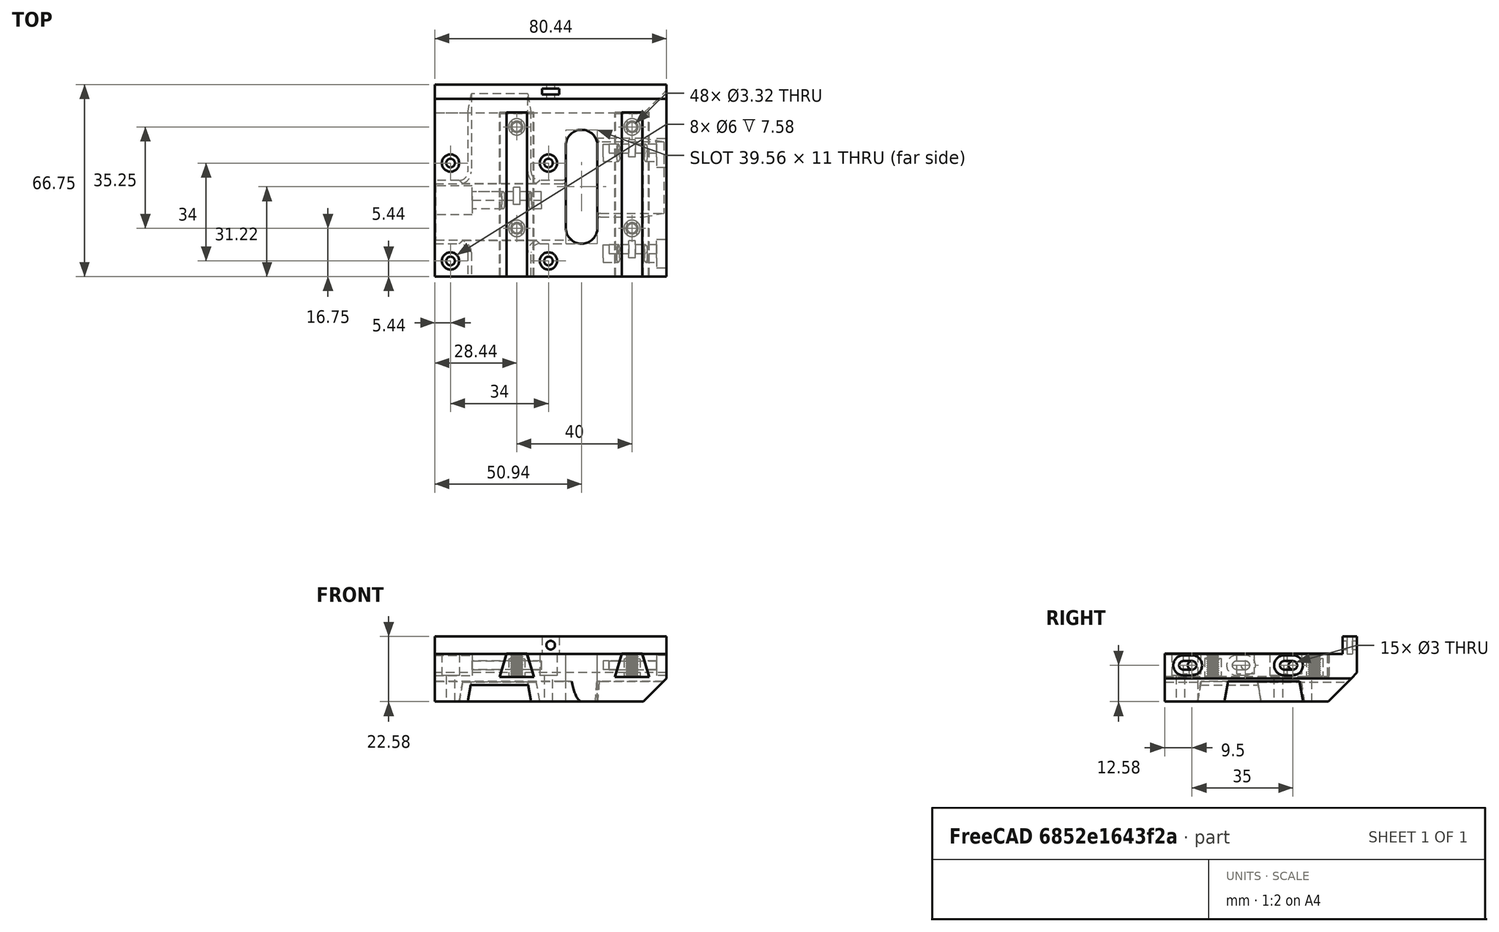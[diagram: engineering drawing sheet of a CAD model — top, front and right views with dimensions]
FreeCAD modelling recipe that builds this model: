
FCSTD DOCUMENT  (FreeCAD 2022.111R28429 (Git))
Label: E2_Adjustable_Plate
License: All rights reserved
LicenseURL: http://en.wikipedia.org/wiki/All_rights_reserved
objects: Sketcher::SketchObject×18, PartDesign::Pocket×16, Sketcher::SketchExport×6, Part::FeaturePython×6, PartDesign::Body×4, PartDesign::FeatureBase×3, Part::SubShapeBinder×2, Part::Extrusion×2, PartDesign::Pad×2, PartDesign::Hole×2, PartDesign::Chamfer×2, PartDesign::SubShapeBinder×1, PartDesign::Fillet×1, Part::Cut×1, App::DocumentObjectGroup×1
note: 115 computed .brp shape members not serialized (recipe doc carries the construction recipe); baked Part::Feature solids carry a one-line shape summary decoded from their .brp

FEATURE [PartDesign::SubShapeBinder] Binder  label="Binder(Pad002)"
  BindCopyOnChange = 0
  BindMode = 0
  ClaimChildren = false
  Context = -> Body001 [Binder.]
  FillStyle = 0
  Fuse = false
  MakeFace = true
  PartialLoad = false
  Refine = true
  Relative = true
  Support = -> [Pad002[Face14]]
  TreeRank = 0
  _Version = 7
FEATURE [Part::SubShapeBinder] Import002  label="Import002(Chamfer002)"
  BindCopyOnChange = 0
  BindMode = 0
  ClaimChildren = false
  FillStyle = 0
  Fuse = false
  MakeFace = false
  PartialLoad = false
  Refine = true
  Relative = true
  Support = -> [Body001[Chamfer002.]]
  TreeRank = 0
  _Version = 7
FEATURE [Part::SubShapeBinder] Import003  label="Import003(M4Holes)"
  BindCopyOnChange = 0
  BindMode = 0
  ClaimChildren = false
  FillStyle = 0
  Fuse = false
  MakeFace = false
  PartialLoad = false
  Refine = true
  Relative = true
  Support = -> [Body001[Export.]]
  TreeRank = 0
  _Version = 7
FEATURE [Sketcher::SketchObject] Sketch015
  ExternalGeometry = -> [Import002,Import003]
  FullyConstrained = true
  Placement = pos=(0,0.1,0) rot=(-1,0,0;4.71239rad)
  TreeRank = 0
  expr: Constraints[20] = Sketch014.Constraints[20]
  expr: Constraints[21] = Sketch014.Constraints[21]
  expr: Constraints[22] = Sketch014.Constraints[22]
  expr: Constraints[23] = Sketch014.Constraints[23]
  expr: Constraints[25] = Sketch014.Constraints[25]
  sketch-geometry (26):
    g0: LineSegment [constr] StartX=28.44 StartY=-3.7e-15 StartZ=0 EndX=28.44 EndY=16.58 EndZ=0
    g1: LineSegment [constr] StartX=68.44 StartY=-3.7e-15 StartZ=0 EndX=68.44 EndY=16.58 EndZ=0
    g2: LineSegment [constr] StartX=24.94 StartY=16.68 StartZ=0 EndX=31.94 EndY=16.68 EndZ=0
    g3: LineSegment [constr] StartX=31.94 StartY=16.68 StartZ=0 EndX=34.44 EndY=8.58 EndZ=0
    g4: LineSegment [constr] StartX=34.44 StartY=8.58 StartZ=0 EndX=22.44 EndY=8.58 EndZ=0
    g5: LineSegment [constr] StartX=22.44 StartY=8.58 StartZ=0 EndX=24.94 EndY=16.68 EndZ=0
    g6: LineSegment [constr] StartX=64.94 StartY=16.68 StartZ=0 EndX=71.94 EndY=16.68 EndZ=0
    g7: LineSegment [constr] StartX=71.94 StartY=16.68 StartZ=0 EndX=74.44 EndY=8.58 EndZ=0
    g8: LineSegment [constr] StartX=74.44 StartY=8.58 StartZ=0 EndX=62.44 EndY=8.58 EndZ=0
    g9: LineSegment [constr] StartX=62.44 StartY=8.58 StartZ=0 EndX=64.94 EndY=16.68 EndZ=0
    g10: LineSegment StartX=22.711 StartY=8.78 StartZ=0 EndX=34.169 EndY=8.78 EndZ=0
    g11: LineSegment StartX=34.169 StartY=8.78 StartZ=0 EndX=31.8233 EndY=16.38 EndZ=0
    g12: LineSegment StartX=31.8233 StartY=16.38 StartZ=0 EndX=25.0567 EndY=16.38 EndZ=0
    g13: LineSegment StartX=25.0567 StartY=16.38 StartZ=0 EndX=22.711 EndY=8.78 EndZ=0
    g14: LineSegment StartX=62.711 StartY=8.78 StartZ=0 EndX=74.169 EndY=8.78 EndZ=0
    g15: LineSegment StartX=74.169 StartY=8.78 StartZ=0 EndX=71.8233 EndY=16.38 EndZ=0
    g16: LineSegment StartX=71.8233 StartY=16.38 StartZ=0 EndX=65.0567 EndY=16.38 EndZ=0
    g17: LineSegment StartX=65.0567 StartY=16.38 StartZ=0 EndX=62.711 EndY=8.78 EndZ=0
    g18: LineSegment [constr] StartX=25.0567 StartY=16.38 StartZ=0 EndX=25.0567 EndY=16.58 EndZ=0
    g19: LineSegment [constr] StartX=25.0567 StartY=16.38 StartZ=0 EndX=24.8656 EndY=16.439 EndZ=0
    g20: LineSegment [constr] StartX=34.169 StartY=8.78 StartZ=0 EndX=34.169 EndY=8.58 EndZ=0
    g21: LineSegment [constr] StartX=34.169 StartY=8.78 StartZ=0 EndX=34.3601 EndY=8.83898 EndZ=0
    g22: LineSegment [constr] StartX=65.0567 StartY=16.38 StartZ=0 EndX=65.0567 EndY=16.58 EndZ=0
    g23: LineSegment [constr] StartX=65.0567 StartY=16.38 StartZ=0 EndX=64.8656 EndY=16.439 EndZ=0
    g24: LineSegment [constr] StartX=74.169 StartY=8.78 StartZ=0 EndX=74.169 EndY=8.58 EndZ=0
    g25: LineSegment [constr] StartX=74.169 StartY=8.78 StartZ=0 EndX=74.3601 EndY=8.83898 EndZ=0
  constraints (74):
    c: PointOnObject(g0,g-6)
    c: Vertical(g0)
    c: PointOnObject(g1,g-6)
    c: Vertical(g1)
    c: Symmetric(g-4,g-4,g1)
    c: Symmetric(g-5,g-5,g0)
    c: Coincident(g2,g3)
    c: Coincident(g3,g4)
    c: Coincident(g4,g5)
    c: Coincident(g5,g2)
    c: Coincident(g6,g7)
    c: Coincident(g7,g8)
    c: Coincident(g8,g9)
    c: Coincident(g9,g6)
    c: Symmetric(g6,g6,g1)
    c: Symmetric(g7,g8,g1)
    c: Symmetric(g2,g2,g0)
    c: Symmetric(g3,g4,g0)
    c: Horizontal(g2,g6)
    c: Equal(g2,g6)
    c: DistanceX(g6,g6) = 7
    c: DistanceY(g-6,g6) = 0.1
    c: DistanceY(g7,g-6) = 8
    c: DistanceX(g8,g8) = 12
    c: Horizontal(g8,g3)
    c: DistanceX(g4,g4) = 12
    c: Horizontal(g10)
    c: Coincident(g10,g11)
    c: Coincident(g11,g12)
    c: Horizontal(g12)
    c: Coincident(g12,g13)
    c: Coincident(g13,g10)
    c: Horizontal(g14)
    c: Coincident(g14,g15)
    c: Coincident(g15,g16)
    c: Horizontal(g16)
    c: Coincident(g16,g17)
    c: Coincident(g17,g14)
    c: Coincident(g18,g12)
    c: PointOnObject(g18,g-6)
    c: Vertical(g18)
    c: Coincident(g19,g12)
    c: PointOnObject(g19,g5)
    c: Coincident(g20,g10)
    c: PointOnObject(g20,g4)
    c: Coincident(g21,g10)
    c: PointOnObject(g21,g3)
    c: Perpendicular(g3,g21)
    c: Perpendicular(g4,g20)
    c: Perpendicular(g5,g19)
    c: Equal(g19,g18)
    c: Equal(g18,g21)
    c: Equal(g21,g20)
    c: Coincident(g22,g16)
    c: PointOnObject(g22,g-6)
    c: Vertical(g22)
    c: Coincident(g23,g16)
    c: PointOnObject(g23,g9)
    c: Coincident(g24,g14)
    c: PointOnObject(g24,g8)
    c: Vertical(g24)
    c: Coincident(g25,g14)
    c: PointOnObject(g25,g7)
    c: Perpendicular(g7,g25)
    c: Perpendicular(g9,g23)
    c: Equal(g23,g22)
    c: Equal(g22,g25)
    c: Equal(g25,g24)
    c: Equal(g22,g20)
    c: Parallel(g11,g3)
    c: Parallel(g5,g13)
    c: Parallel(g17,g9)
    c: Parallel(g15,g7)
    c: DistanceY(g20,g20) = 0.2
FEATURE [Part::Extrusion] Extrude001
  Base = -> Sketch015
  Dir = (0,-1,-2e-16)
  DirMode = 2
  FaceMakerClass = Part::FaceMakerBullseye
  InnerTaperAngle = 0
  InnerTaperAngleRev = 0
  LengthFwd = 56.5
  LengthRev = 0
  Linearize = true
  Reversed = true
  Solid = true
  Symmetric = false
  TreeRank = 0
FEATURE [PartDesign::Body] Body001  label="Slice.0"
  AutoGroupSolids = false
  ExportMode = 0
  Group = -> [Sketch004,Pad002,Binder,Sketch005,Pad003,Sketch006,Pocket003,Sketch007,Sketch009,Pocket006,Pocket007,Sketch011,Pocket,Pocket009,Hole,Export,Sketch013,Pocket010,Pocket011,Pocket012,Hole001,Chamfer001,Chamfer002,Sketch016,Sketch017,Export001,Export002,Export003,Export004,Sketch,Pocket013,Fillet,Export005,Pocket014]
  Origin = -> Origin001
  Tip = -> Pocket014
  TreeRank = 0
  _ExportChildren = -> [Pad002,Binder,Pad003,Pocket003,Pocket006,Pocket007,Pocket,Pocket009,Hole,Pocket010,Pocket011,Pocket012,Hole001,Chamfer001,Chamfer002,Pocket013,Fillet,Pocket014]
  _GroupVersion = 1
FEATURE [Sketcher::SketchObject] Sketch004
  Exports = -> [Export]
  FullyConstrained = true
  MapMode = 5
  Support = -> [XY_Plane001]
  TreeRank = 0
  sketch-geometry (40):
    g0: LineSegment StartX=0 StartY=0 StartZ=0 EndX=80.44 EndY=0 EndZ=0
    g1: LineSegment StartX=80.44 StartY=0 StartZ=0 EndX=80.44 EndY=66.75 EndZ=0
    g2: LineSegment StartX=80.44 StartY=66.75 StartZ=0 EndX=0 EndY=66.75 EndZ=0
    g3: LineSegment StartX=0 StartY=66.75 StartZ=0 EndX=0 EndY=0 EndZ=0
    g4: Circle CenterX=5.44 CenterY=5.44 CenterZ=0 NormalX=0 NormalY=0 NormalZ=1 AngleXU=0 Radius=1.5
    g5: Circle CenterX=39.44 CenterY=5.44 CenterZ=0 NormalX=0 NormalY=0 NormalZ=1 AngleXU=0 Radius=1.5
    g6: Circle CenterX=5.44 CenterY=39.44 CenterZ=0 NormalX=0 NormalY=0 NormalZ=1 AngleXU=0 Radius=1.5
    g7: Circle CenterX=39.44 CenterY=39.44 CenterZ=0 NormalX=0 NormalY=0 NormalZ=1 AngleXU=0 Radius=1.5
    g8: LineSegment [constr] StartX=5.44 StartY=39.44 StartZ=0 EndX=39.44 EndY=39.44 EndZ=0
    g9: LineSegment [constr] StartX=39.44 StartY=39.44 StartZ=0 EndX=39.44 EndY=5.44 EndZ=0
    g10: LineSegment [constr] StartX=39.44 StartY=5.44 StartZ=0 EndX=5.44 EndY=5.44 EndZ=0
    g11: LineSegment [constr] StartX=5.44 StartY=5.44 StartZ=0 EndX=5.44 EndY=39.44 EndZ=0
    g12: Circle [constr] CenterX=28.44 CenterY=52 CenterZ=0 NormalX=0 NormalY=0 NormalZ=1 AngleXU=0 Radius=1.5
    g13: Circle [constr] CenterX=28.44 CenterY=16.75 CenterZ=0 NormalX=0 NormalY=0 NormalZ=1 AngleXU=0 Radius=1.5
    g14: Circle [constr] CenterX=68.44 CenterY=52 CenterZ=0 NormalX=0 NormalY=0 NormalZ=1 AngleXU=0 Radius=1.5
    g15: Circle [constr] CenterX=68.44 CenterY=16.75 CenterZ=0 NormalX=0 NormalY=0 NormalZ=1 AngleXU=0 Radius=1.5
    g16: LineSegment [constr] StartX=28.44 StartY=52 StartZ=0 EndX=68.44 EndY=52 EndZ=0
    g17: LineSegment [constr] StartX=68.44 StartY=52 StartZ=0 EndX=68.44 EndY=16.75 EndZ=0
    g18: LineSegment [constr] StartX=68.44 StartY=16.75 StartZ=0 EndX=28.44 EndY=16.75 EndZ=0
    g19: LineSegment [constr] StartX=28.44 StartY=16.75 StartZ=0 EndX=28.44 EndY=52 EndZ=0
    g20: LineSegment [constr] StartX=22.44 StartY=0 StartZ=0 EndX=34.44 EndY=0 EndZ=0
    g21: LineSegment [constr] StartX=34.44 StartY=0 StartZ=0 EndX=34.44 EndY=57 EndZ=0
    g22: LineSegment [constr] StartX=34.44 StartY=57 StartZ=0 EndX=22.44 EndY=57 EndZ=0
    g23: LineSegment [constr] StartX=22.44 StartY=57 StartZ=0 EndX=22.44 EndY=0 EndZ=0
    g24: LineSegment [constr] StartX=62.44 StartY=0 StartZ=0 EndX=74.44 EndY=0 EndZ=0
    g25: LineSegment [constr] StartX=74.44 StartY=0 StartZ=0 EndX=74.44 EndY=57 EndZ=0
    g26: LineSegment [constr] StartX=74.44 StartY=57 StartZ=0 EndX=62.44 EndY=57 EndZ=0
    g27: LineSegment [constr] StartX=62.44 StartY=57 StartZ=0 EndX=62.44 EndY=0 EndZ=0
    g28: LineSegment [constr] StartX=28.44 StartY=52 StartZ=0 EndX=28.44 EndY=57 EndZ=0
    g29: LineSegment [constr] StartX=68.44 StartY=52 StartZ=0 EndX=68.44 EndY=57 EndZ=0
    g30: ArcOfCircle CenterX=50.94 CenterY=45.5 CenterZ=0 NormalX=0 NormalY=0 NormalZ=1 AngleXU=0 Radius=5.5 StartAngle=0 EndAngle=3.14159
    g31: ArcOfCircle CenterX=50.94 CenterY=16.94 CenterZ=0 NormalX=0 NormalY=0 NormalZ=1 AngleXU=0 Radius=5.5 StartAngle=3.14159 EndAngle=6.28319
    g32: LineSegment StartX=45.44 StartY=45.5 StartZ=0 EndX=45.44 EndY=16.94 EndZ=0
    g33: LineSegment StartX=56.44 StartY=45.5 StartZ=0 EndX=56.44 EndY=16.94 EndZ=0
    g34: LineSegment [constr] StartX=45.44 StartY=16.94 StartZ=0 EndX=39.44 EndY=16.94 EndZ=0
    g35: LineSegment [constr] StartX=56.44 StartY=16.94 StartZ=0 EndX=62.44 EndY=16.94 EndZ=0
    g36: LineSegment [constr] StartX=34.44 StartY=57 StartZ=0 EndX=62.44 EndY=57 EndZ=0
    g37: LineSegment [constr] StartX=50.94 StartY=57 StartZ=0 EndX=50.94 EndY=51 EndZ=0
    g38: LineSegment [constr] StartX=39.44 StartY=5.44 StartZ=0 EndX=62.44 EndY=5.44 EndZ=0
    g39: LineSegment [constr] StartX=50.94 StartY=5.44 StartZ=0 EndX=50.94 EndY=11.44 EndZ=0
  constraints (108):
    c: Coincident(g0,g1)
    c: Coincident(g1,g2)
    c: Coincident(g2,g3)
    c: Coincident(g3,g0)
    c: Horizontal(g0)
    c: Horizontal(g2)
    c: Vertical(g1)
    c: Vertical(g3)
    c: Coincident(g0,g-1)
    c: DistanceY(g3,g3) = 66.75
    c: Coincident(g8,g9)
    c: Coincident(g9,g10)
    c: Coincident(g10,g11)
    c: Coincident(g11,g8)
    c: Horizontal(g8)
    c: Horizontal(g10)
    c: Vertical(g9)
    c: Vertical(g11)
    c: Coincident(g8,g6)
    c: Coincident(g9,g5)
    c: Coincident(g7,g8)
    c: Coincident(g4,g10)
    c: Equal(g10,g11)
    c: DistanceY(g11,g11) = 34
    c: DistanceX(g0,g4) = 5.44
    c: DistanceY(g0,g4) = 5.44
    c: Diameter(g4) = 3
    c: Equal(g4,g5)
    c: Equal(g4,g7)
    c: Equal(g4,g6)
    c: Coincident(g16,g17)
    c: Coincident(g17,g18)
    c: Coincident(g18,g19)
    c: Coincident(g19,g16)
    c: Horizontal(g16)
    c: Horizontal(g18)
    c: Vertical(g17)
    c: Vertical(g19)
    c: Coincident(g16,g12)
    c: Coincident(g17,g15)
    c: Coincident(g13,g18)
    c: Coincident(g14,g16)
    c: DistanceX(g16,g16) = 40
    c: DistanceY(g17,g17) = 35.25
    c: Diameter(g13) = 3
    c: Equal(g13,g15)
    c: Equal(g13,g14)
    c: Equal(g13,g12)
    c: DistanceY(g0,g13) = 16.75
    c: DistanceX(g4,g13) = 23
    c: DistanceX(g15,g0) = 12
    c: Coincident(g20,g21)
    c: Coincident(g21,g22)
    c: Coincident(g22,g23)
    c: Coincident(g23,g20)
    c: Horizontal(g20)
    c: Horizontal(g22)
    c: Vertical(g21)
    c: Vertical(g23)
    c: PointOnObject(g20,g0)
    c: Coincident(g24,g25)
    c: Coincident(g25,g26)
    c: Coincident(g26,g27)
    c: Coincident(g27,g24)
    c: Horizontal(g24)
    c: Horizontal(g26)
    c: Vertical(g25)
    c: Vertical(g27)
    c: PointOnObject(g24,g0)
    c: Equal(g22,g26)
    c: DistanceX(g26,g26) = 12
    c: DistanceY(g25,g25) = 57
    c: Horizontal(g26,g21)
    c: Coincident(g28,g12)
    c: Vertical(g28)
    c: Coincident(g29,g14)
    c: Vertical(g29)
    c: Symmetric(g26,g25,g29)
    c: Symmetric(g22,g21,g28)
    c: Tangent(g30,g33) = 1.5708
    c: Tangent(g30,g32) = -1.5708
    c: Tangent(g32,g31) = -1.5708
    c: Tangent(g33,g31) = 1.5708
    c: Vertical(g32)
    c: Coincident(g34,g31)
    c: PointOnObject(g34,g9)
    c: Coincident(g35,g31)
    c: PointOnObject(g35,g27)
    c: Horizontal(g35)
    c: Horizontal(g34)
    c: Equal(g34,g35)
    c: DistanceX(g35,g35) = 6
    c: Vertical(g33)
    c: Coincident(g36,g21)
    c: Coincident(g36,g26)
    c: PointOnObject(g37,g36)
    c: PointOnObject(g37,g30)
    c: Vertical(g37)
    c: Vertical(g37,g30)
    c: Equal(g37,g35)
    c: Coincident(g38,g5)
    c: PointOnObject(g38,g27)
    c: Horizontal(g38)
    c: PointOnObject(g39,g38)
    c: PointOnObject(g39,g31)
    c: Vertical(g39)
    c: Vertical(g39,g31)
    c: Equal(g34,g39)
FEATURE [PartDesign::Pad] Pad002
  ClaimChildren = false
  Direction = (1,1,1)
  Fit = 0
  FitJoin = 0
  InnerFit = 0
  InnerFitJoin = 0
  InnerTaperAngle = 0
  InnerTaperAngleRev = 0
  Length = 16.58
  Length2 = 100
  Linearize = true
  NewSolid = false
  Profile = -> Sketch004
  Refine = true
  Suppress = false
  TreeRank = 0
  Type = 0
  _ProfileBasedVersion = 1
FEATURE [Sketcher::SketchObject] Sketch005
  ExternalGeometry = -> [Pad002]
  FullyConstrained = true
  MapMode = 5
  Placement = pos=(0,0,16.58) rot=(0,0,1;0rad)
  Support = -> [Binder]
  TreeRank = 0
  sketch-geometry (4):
    g0: LineSegment StartX=0 StartY=66.75 StartZ=0 EndX=80.44 EndY=66.75 EndZ=0
    g1: LineSegment StartX=80.44 StartY=66.75 StartZ=0 EndX=80.44 EndY=61.75 EndZ=0
    g2: LineSegment StartX=80.44 StartY=61.75 StartZ=0 EndX=0 EndY=61.75 EndZ=0
    g3: LineSegment StartX=0 StartY=61.75 StartZ=0 EndX=0 EndY=66.75 EndZ=0
  constraints (10):
    c: Coincident(g0,g1)
    c: Coincident(g1,g2)
    c: Coincident(g2,g3)
    c: Coincident(g3,g0)
    c: Horizontal(g2)
    c: Vertical(g1)
    c: Vertical(g3)
    c: Coincident(g0,g-3)
    c: Coincident(g0,g-3)
    c: DistanceY(g1,g1) = 5
FEATURE [PartDesign::Pad] Pad003
  BaseFeature = -> Pad002
  ClaimChildren = false
  Direction = (1,1,1)
  Fit = 0
  FitJoin = 0
  InnerFit = 0
  InnerFitJoin = 0
  InnerTaperAngle = 0
  InnerTaperAngleRev = 0
  Length = 6
  Length2 = 100
  Linearize = true
  NewSolid = false
  Profile = -> Sketch005
  Refine = true
  Suppress = false
  TreeRank = 0
  Type = 0
  _ProfileBasedVersion = 1
FEATURE [Sketcher::SketchObject] Sketch006
  ExternalGeometry = -> [Pad003]
  FullyConstrained = true
  MapMode = 5
  Placement = pos=(0,66.75,0) rot=(0,0.707107,0.707107;3.14159rad)
  Support = -> [Pad003]
  TreeRank = 0
  sketch-geometry (2):
    g0: Circle CenterX=-40.22 CenterY=19.58 CenterZ=0 NormalX=0 NormalY=0 NormalZ=1 AngleXU=0 Radius=1.5
    g1: LineSegment [constr] StartX=-40.22 StartY=19.58 StartZ=0 EndX=-40.22 EndY=22.58 EndZ=0
  constraints (5):
    c: Diameter(g0) = 3
    c: Coincident(g1,g0)
    c: Vertical(g1)
    c: DistanceY(g1,g1) = 3
    c: Symmetric(g-3,g-3,g1)
FEATURE [PartDesign::Pocket] Pocket003
  BaseFeature = -> Pad003
  ClaimChildren = false
  Fit = 0
  FitJoin = 0
  InnerFit = 0
  InnerFitJoin = 0
  InnerTaperAngle = 0
  InnerTaperAngleRev = 0
  Length = 5
  Length2 = 100
  Linearize = true
  NewSolid = false
  Profile = -> Sketch006
  Refine = true
  Suppress = false
  TreeRank = 0
  Type = 2
  _ProfileBasedVersion = 1
FEATURE [Sketcher::SketchObject] Sketch007
  ExternalGeometry = -> [Pocket003]
  FullyConstrained = true
  MapMode = 5
  Placement = pos=(0,0,22.58) rot=(0,0,1;0rad)
  Support = -> [Pocket003]
  TreeRank = 0
  sketch-geometry (8):
    g0: LineSegment StartX=37.22 StartY=65.25 StartZ=0 EndX=43.22 EndY=65.25 EndZ=0
    g1: LineSegment StartX=43.22 StartY=65.25 StartZ=0 EndX=43.22 EndY=63.25 EndZ=0
    g2: LineSegment StartX=43.22 StartY=63.25 StartZ=0 EndX=37.22 EndY=63.25 EndZ=0
    g3: LineSegment StartX=37.22 StartY=63.25 StartZ=0 EndX=37.22 EndY=65.25 EndZ=0
    g4: LineSegment [constr] StartX=40.22 StartY=66.75 StartZ=0 EndX=40.22 EndY=64.25 EndZ=0
    g5: LineSegment [constr] StartX=40.22 StartY=64.25 StartZ=0 EndX=40.22 EndY=61.75 EndZ=0
    g6: LineSegment [constr] StartX=40.22 StartY=64.25 StartZ=0 EndX=37.22 EndY=64.25 EndZ=0
    g7: LineSegment [constr] StartX=40.22 StartY=64.25 StartZ=0 EndX=43.22 EndY=64.25 EndZ=0
  constraints (23):
    c: Coincident(g0,g1)
    c: Coincident(g1,g2)
    c: Coincident(g2,g3)
    c: Coincident(g3,g0)
    c: Horizontal(g0)
    c: Horizontal(g2)
    c: Vertical(g1)
    c: Vertical(g3)
    c: DistanceY(g1,g1) = 2
    c: DistanceX(g0,g0) = 6
    c: Vertical(g4)
    c: Coincident(g5,g4)
    c: PointOnObject(g5,g-4)
    c: Vertical(g5)
    c: Coincident(g6,g4)
    c: PointOnObject(g6,g3)
    c: Coincident(g7,g4)
    c: Horizontal(g7)
    c: Horizontal(g6)
    c: Equal(g6,g7)
    c: Equal(g5,g4)
    c: Symmetric(g1,g0,g7)
    c: Symmetric(g-3,g-3,g4)
FEATURE [Sketcher::SketchObject] Sketch009
  Exports = -> [Export001,Export002]
  FullyConstrained = true
  MapMode = 5
  Placement = pos=(0,0,0) rot=(0.57735,-0.57735,-0.57735;2.0944rad)
  Support = -> [Pocket003]
  TreeRank = 0
  sketch-geometry (9):
    g0: ArcOfCircle [constr] CenterX=-28 CenterY=12.58 CenterZ=0 NormalX=0 NormalY=0 NormalZ=1 AngleXU=0 Radius=1.5 StartAngle=1.5708 EndAngle=4.71239
    g1: ArcOfCircle [constr] CenterX=-25 CenterY=12.58 CenterZ=0 NormalX=0 NormalY=0 NormalZ=1 AngleXU=0 Radius=1.5 StartAngle=4.71239 EndAngle=7.85398
    g2: LineSegment [constr] StartX=-28 StartY=11.08 StartZ=0 EndX=-25 EndY=11.08 EndZ=0
    g3: LineSegment [constr] StartX=-28 StartY=14.08 StartZ=0 EndX=-25 EndY=14.08 EndZ=0
    g4: ArcOfCircle CenterX=-28 CenterY=12.58 CenterZ=0 NormalX=0 NormalY=0 NormalZ=1 AngleXU=0 Radius=3.5 StartAngle=1.5708 EndAngle=4.71239
    g5: ArcOfCircle CenterX=-25 CenterY=12.58 CenterZ=0 NormalX=0 NormalY=0 NormalZ=1 AngleXU=0 Radius=3.5 StartAngle=4.71239 EndAngle=7.85398
    g6: LineSegment StartX=-28 StartY=9.08 StartZ=0 EndX=-25 EndY=9.08 EndZ=0
    g7: LineSegment StartX=-28 StartY=16.08 StartZ=0 EndX=-25 EndY=16.08 EndZ=0
    g8: Circle [constr] CenterX=-28 CenterY=12.58 CenterZ=0 NormalX=0 NormalY=0 NormalZ=1 AngleXU=0 Radius=1.5
  constraints (20):
    c: Tangent(g0,g3) = 1.5708
    c: Tangent(g0,g2) = -1.5708
    c: Tangent(g2,g1) = -1.5708
    c: Tangent(g3,g1) = 1.5708
    c: Horizontal(g2)
    c: Equal(g0,g1)
    c: Tangent(g4,g7) = 1.5708
    c: Tangent(g4,g6) = -1.5708
    c: Tangent(g6,g5) = -1.5708
    c: Tangent(g7,g5) = 1.5708
    c: Horizontal(g6)
    c: Coincident(g4,g0)
    c: Coincident(g1,g5)
    c: Diameter(g1) = 3
    c: Diameter(g5) = 7
    c: DistanceX(g0,g1) = 3
    c: DistanceX(g1,g-1) = 25
    c: DistanceY(g-1,g1) = 12.58
    c: Coincident(g8,g0)
    c: Equal(g8,g0)
FEATURE [PartDesign::Pocket] Pocket006
  BaseFeature = -> Pocket003
  ClaimChildren = false
  Fit = 0
  FitJoin = 0
  InnerFit = 0
  InnerFitJoin = 0
  InnerTaperAngle = 0
  InnerTaperAngleRev = 0
  Length = 6
  Length2 = 100
  Linearize = true
  NewSolid = false
  Profile = -> Sketch007
  Refine = true
  Suppress = false
  TreeRank = 0
  Type = 0
  _ProfileBasedVersion = 1
FEATURE [PartDesign::Pocket] Pocket007
  BaseFeature = -> Pocket006
  ClaimChildren = false
  Fit = 0
  FitJoin = 0
  InnerFit = 0
  InnerFitJoin = 0
  InnerTaperAngle = 0
  InnerTaperAngleRev = 0
  Length = 13
  Length2 = 100
  Linearize = true
  NewSolid = false
  Profile = -> Sketch009
  Refine = true
  Suppress = false
  TreeRank = 0
  Type = 0
  _ProfileBasedVersion = 1
FEATURE [Sketcher::SketchObject] Sketch011
  Exports = -> [Export003,Export004]
  FullyConstrained = true
  MapMode = 5
  Placement = pos=(80.44,0,0) rot=(0.57735,0.57735,0.57735;2.0944rad)
  Support = -> [Pocket007]
  TreeRank = 0
  sketch-geometry (18):
    g0: ArcOfCircle [constr] CenterX=6.5 CenterY=12.58 CenterZ=0 NormalX=0 NormalY=0 NormalZ=1 AngleXU=0 Radius=1.5 StartAngle=1.5708 EndAngle=4.71239
    g1: ArcOfCircle [constr] CenterX=9.5 CenterY=12.58 CenterZ=0 NormalX=0 NormalY=0 NormalZ=1 AngleXU=0 Radius=1.5 StartAngle=4.71239 EndAngle=7.85398
    g2: LineSegment [constr] StartX=6.5 StartY=11.08 StartZ=0 EndX=9.5 EndY=11.08 EndZ=0
    g3: LineSegment [constr] StartX=6.5 StartY=14.08 StartZ=0 EndX=9.5 EndY=14.08 EndZ=0
    g4: ArcOfCircle CenterX=6.5 CenterY=12.58 CenterZ=0 NormalX=0 NormalY=0 NormalZ=1 AngleXU=0 Radius=3.5 StartAngle=1.5708 EndAngle=4.71239
    g5: ArcOfCircle CenterX=9.5 CenterY=12.58 CenterZ=0 NormalX=0 NormalY=0 NormalZ=1 AngleXU=0 Radius=3.5 StartAngle=4.71239 EndAngle=7.85398
    g6: LineSegment StartX=6.5 StartY=9.08 StartZ=0 EndX=9.5 EndY=9.08 EndZ=0
    g7: LineSegment StartX=6.5 StartY=16.08 StartZ=0 EndX=9.5 EndY=16.08 EndZ=0
    g8: ArcOfCircle [constr] CenterX=41.5 CenterY=12.58 CenterZ=0 NormalX=0 NormalY=0 NormalZ=1 AngleXU=0 Radius=1.5 StartAngle=1.5708 EndAngle=4.71239
    g9: ArcOfCircle [constr] CenterX=44.5 CenterY=12.58 CenterZ=0 NormalX=0 NormalY=0 NormalZ=1 AngleXU=0 Radius=1.5 StartAngle=4.71239 EndAngle=7.85398
    g10: LineSegment [constr] StartX=41.5 StartY=11.08 StartZ=0 EndX=44.5 EndY=11.08 EndZ=0
    g11: LineSegment [constr] StartX=41.5 StartY=14.08 StartZ=0 EndX=44.5 EndY=14.08 EndZ=0
    g12: ArcOfCircle CenterX=41.5 CenterY=12.58 CenterZ=0 NormalX=0 NormalY=0 NormalZ=1 AngleXU=0 Radius=3.5 StartAngle=1.5708 EndAngle=4.71239
    g13: ArcOfCircle CenterX=44.5 CenterY=12.58 CenterZ=0 NormalX=0 NormalY=0 NormalZ=1 AngleXU=0 Radius=3.5 StartAngle=4.71239 EndAngle=7.85398
    g14: LineSegment StartX=41.5 StartY=9.08 StartZ=0 EndX=44.5 EndY=9.08 EndZ=0
    g15: LineSegment StartX=41.5 StartY=16.08 StartZ=0 EndX=44.5 EndY=16.08 EndZ=0
    g16: Circle [constr] CenterX=9.5 CenterY=12.58 CenterZ=0 NormalX=0 NormalY=0 NormalZ=1 AngleXU=0 Radius=1.5
    g17: Circle [constr] CenterX=44.5 CenterY=12.58 CenterZ=0 NormalX=0 NormalY=0 NormalZ=1 AngleXU=0 Radius=1.5
  constraints (40):
    c: Tangent(g0,g3) = 1.5708
    c: Tangent(g0,g2) = -1.5708
    c: Tangent(g2,g1) = -1.5708
    c: Tangent(g3,g1) = 1.5708
    c: Horizontal(g2)
    c: Equal(g0,g1)
    c: Tangent(g4,g7) = 1.5708
    c: Tangent(g4,g6) = -1.5708
    c: Tangent(g6,g5) = -1.5708
    c: Tangent(g7,g5) = 1.5708
    c: Horizontal(g6)
    c: Coincident(g4,g0)
    c: Tangent(g8,g11) = 1.5708
    c: Tangent(g8,g10) = -1.5708
    c: Tangent(g10,g9) = -1.5708
    c: Tangent(g11,g9) = 1.5708
    c: Horizontal(g10)
    c: Equal(g8,g9)
    c: Tangent(g12,g15) = 1.5708
    c: Tangent(g12,g14) = -1.5708
    c: Tangent(g14,g13) = -1.5708
    c: Tangent(g15,g13) = 1.5708
    c: Horizontal(g14)
    c: Coincident(g12,g8)
    c: Coincident(g9,g13)
    c: Coincident(g1,g5)
    c: Horizontal(g1,g8)
    c: Diameter(g1) = 3
    c: Equal(g1,g8)
    c: Diameter(g5) = 7
    c: Equal(g5,g12)
    c: DistanceX(g8,g9) = 3
    c: DistanceX(g0,g1) = 3
    c: DistanceX(g-1,g0) = 6.5
    c: DistanceX(g-1,g8) = 41.5
    c: DistanceY(g-1,g0) = 12.58
    c: Coincident(g16,g5)
    c: Equal(g16,g1)
    c: Coincident(g17,g13)
    c: Equal(g17,g9)
FEATURE [PartDesign::Pocket] Pocket009
  BaseFeature = -> Pocket
  ClaimChildren = false
  Fit = 0
  FitJoin = 0
  InnerFit = 0
  InnerFitJoin = 0
  InnerTaperAngle = 0
  InnerTaperAngleRev = 0
  Length = 3.5
  Length2 = 100
  Linearize = true
  NewSolid = false
  Profile = -> Sketch011
  Refine = true
  Suppress = false
  TreeRank = 0
  Type = 0
  _ProfileBasedVersion = 1
FEATURE [PartDesign::Hole] Hole
  BaseFeature = -> Pocket009
  ClaimChildren = false
  CustomThreadClearance = 0
  Depth = 7.58
  DepthType = 0
  Diameter = 6
  DrillForDepth = false
  DrillPoint = 0
  DrillPointAngle = 118
  Fit = 0
  FitJoin = 0
  HoleCutCountersinkAngle = 90
  HoleCutCustomValues = false
  HoleCutDepth = 0
  HoleCutDiameter = 6.1
  HoleCutType = 0
  InnerFit = 0
  InnerFitJoin = 0
  ModelThread = false
  NewSolid = false
  Profile = -> Pocket009 [Edge39,Edge44,Vertex33,Edge37,Edge38]
  Refine = true
  Suppress = false
  Tapered = false
  TaperedAngle = 90
  ThreadClass = 0
  ThreadDepth = 7.58
  ThreadDepthType = 0
  ThreadDirection = 0
  ThreadFit = 0
  ThreadSize = 0
  ThreadType = 0
  Threaded = false
  TreeRank = 0
  UseCustomThreadClearance = false
  _ProfileBasedVersion = 1
FEATURE [Sketcher::SketchExport] Export  label="M4Holes"
  Base = -> Sketch004
  BaseRefs = -> Sketch004 [edge13,edge15,edge16,edge14]
  Refs = ;g13.edge13 | ;g15.edge15 | ;g16.edge16 | ;g14.edge14
  SyncPlacement = true
  TreeRank = 0
FEATURE [Sketcher::SketchObject] Sketch013
  ExternalGeometry = -> [Export]
  FullyConstrained = true
  MapMode = 5
  Placement = pos=(0,0,16.58) rot=(0,0,1;0rad)
  Support = -> [Hole]
  TreeRank = 0
  sketch-geometry (4):
    g0: Circle CenterX=68.44 CenterY=16.75 CenterZ=0 NormalX=0 NormalY=0 NormalZ=1 AngleXU=0 Radius=1.5
    g1: Circle CenterX=28.44 CenterY=16.75 CenterZ=0 NormalX=0 NormalY=0 NormalZ=1 AngleXU=0 Radius=1.5
    g2: Circle CenterX=68.44 CenterY=52 CenterZ=0 NormalX=0 NormalY=0 NormalZ=1 AngleXU=0 Radius=1.5
    g3: Circle CenterX=28.44 CenterY=52 CenterZ=0 NormalX=0 NormalY=0 NormalZ=1 AngleXU=0 Radius=1.5
  constraints (8):
    c: Coincident(g0,g-4)
    c: Coincident(g1,g-3)
    c: Coincident(g2,g-5)
    c: Equal(g2,g-5)
    c: Equal(g-4,g0)
    c: Equal(g-3,g1)
    c: Coincident(g3,g-6)
    c: Equal(g-6,g3)
FEATURE [PartDesign::Hole] Hole001
  BaseFeature = -> Pocket012
  ClaimChildren = false
  CustomThreadClearance = 0
  Depth = 8
  DepthType = 0
  Diameter = 3.322
  DrillForDepth = false
  DrillPoint = 0
  DrillPointAngle = 118
  Fit = 0
  FitJoin = 0
  HoleCutCountersinkAngle = 90
  HoleCutCustomValues = false
  HoleCutDepth = 0
  HoleCutDiameter = 6.1
  HoleCutType = 0
  InnerFit = 0
  InnerFitJoin = 0
  ModelThread = true
  NewSolid = false
  Profile = -> Sketch013
  Refine = true
  Suppress = false
  Tapered = false
  TaperedAngle = 90
  ThreadClass = 0
  ThreadDepth = 8
  ThreadDepthType = 0
  ThreadDirection = 0
  ThreadFit = 0
  ThreadSize = 11
  ThreadType = 1
  Threaded = true
  TreeRank = 0
  UseCustomThreadClearance = false
  _ProfileBasedVersion = 1
FEATURE [PartDesign::Chamfer] Chamfer001
  Angle = 45
  Base = -> Hole001 [Edge14]
  BaseFeature = -> Hole001
  ChamferType = 0
  FlipDirection = false
  NewSolid = false
  Refine = true
  Size = 8
  Size2 = 1
  SupportTransform = false
  Suppress = false
  TreeRank = 0
FEATURE [PartDesign::Chamfer] Chamfer002
  Angle = 45
  Base = -> Chamfer001 [Edge64]
  BaseFeature = -> Chamfer001
  ChamferType = 0
  FlipDirection = false
  NewSolid = false
  Refine = true
  Size = 10
  Size2 = 1
  SupportTransform = false
  Suppress = false
  TreeRank = 0
FEATURE [Sketcher::SketchObject] Sketch014
  ExternalGeometry = -> [Import002,Import003]
  FullyConstrained = true
  MapMode = 5
  Placement = pos=(0,0,0) rot=(1,0,0;1.5708rad)
  Support = -> [Chamfer002]
  TreeRank = 0
  sketch-geometry (10):
    g0: LineSegment [constr] StartX=28.44 StartY=3.7e-15 StartZ=0 EndX=28.44 EndY=16.58 EndZ=0
    g1: LineSegment [constr] StartX=68.44 StartY=3.7e-15 StartZ=0 EndX=68.44 EndY=16.58 EndZ=0
    g2: LineSegment StartX=24.94 StartY=16.68 StartZ=0 EndX=31.94 EndY=16.68 EndZ=0
    g3: LineSegment StartX=31.94 StartY=16.68 StartZ=0 EndX=34.44 EndY=8.58 EndZ=0
    g4: LineSegment StartX=34.44 StartY=8.58 StartZ=0 EndX=22.44 EndY=8.58 EndZ=0
    g5: LineSegment StartX=22.44 StartY=8.58 StartZ=0 EndX=24.94 EndY=16.68 EndZ=0
    g6: LineSegment StartX=64.94 StartY=16.68 StartZ=0 EndX=71.94 EndY=16.68 EndZ=0
    g7: LineSegment StartX=71.94 StartY=16.68 StartZ=0 EndX=74.44 EndY=8.58 EndZ=0
    g8: LineSegment StartX=74.44 StartY=8.58 StartZ=0 EndX=62.44 EndY=8.58 EndZ=0
    g9: LineSegment StartX=62.44 StartY=8.58 StartZ=0 EndX=64.94 EndY=16.68 EndZ=0
  constraints (26):
    c: PointOnObject(g0,g-6)
    c: Vertical(g0)
    c: PointOnObject(g1,g-6)
    c: Vertical(g1)
    c: Symmetric(g-4,g-4,g1)
    c: Symmetric(g-5,g-5,g0)
    c: Coincident(g2,g3)
    c: Coincident(g3,g4)
    c: Coincident(g4,g5)
    c: Coincident(g5,g2)
    c: Coincident(g6,g7)
    c: Coincident(g7,g8)
    c: Coincident(g8,g9)
    c: Coincident(g9,g6)
    c: Symmetric(g6,g6,g1)
    c: Symmetric(g7,g8,g1)
    c: Symmetric(g2,g2,g0)
    c: Symmetric(g3,g4,g0)
    c: Horizontal(g2,g6)
    c: Equal(g2,g6)
    c: DistanceX(g6,g6) = 7
    c: DistanceY(g-6,g6) = 0.1
    c: DistanceY(g7,g-6) = 8
    c: DistanceX(g8,g8) = 12
    c: Horizontal(g8,g3)
    c: DistanceX(g4,g4) = 12
FEATURE [Sketcher::SketchObject] Sketch016
  AttachmentOffset = pos=(0,0,-12) rot=(0,0,1;0rad)
  ExternalGeometry = -> [Chamfer002,Export004]
  FullyConstrained = true
  MapMode = 5
  Placement = pos=(68.44,0,0) rot=(0.57735,0.57735,0.57735;2.0944rad)
  Support = -> [Chamfer002]
  TreeRank = 0
  sketch-geometry (10):
    g0: LineSegment StartX=6.5 StartY=16.58 StartZ=0 EndX=12.5 EndY=16.58 EndZ=0
    g1: LineSegment StartX=12.5 StartY=16.58 StartZ=0 EndX=12.5 EndY=9.58 EndZ=0
    g2: LineSegment StartX=12.5 StartY=9.58 StartZ=0 EndX=6.5 EndY=9.58 EndZ=0
    g3: LineSegment StartX=6.5 StartY=9.58 StartZ=0 EndX=6.5 EndY=16.58 EndZ=0
    g4: LineSegment StartX=41.5 StartY=16.58 StartZ=0 EndX=47.5 EndY=16.58 EndZ=0
    g5: LineSegment StartX=47.5 StartY=16.58 StartZ=0 EndX=47.5 EndY=9.58 EndZ=0
    g6: LineSegment StartX=47.5 StartY=9.58 StartZ=0 EndX=41.5 EndY=9.58 EndZ=0
    g7: LineSegment StartX=41.5 StartY=9.58 StartZ=0 EndX=41.5 EndY=16.58 EndZ=0
    g8: LineSegment [constr] StartX=44.5 StartY=9.58 StartZ=0 EndX=44.5 EndY=16.58 EndZ=0
    g9: LineSegment [constr] StartX=9.5 StartY=9.58 StartZ=0 EndX=9.5 EndY=16.58 EndZ=0
  constraints (30):
    c: Coincident(g0,g1)
    c: Coincident(g1,g2)
    c: Coincident(g2,g3)
    c: Coincident(g3,g0)
    c: Horizontal(g0)
    c: Horizontal(g2)
    c: Vertical(g1)
    c: Vertical(g3)
    c: Coincident(g4,g5)
    c: Coincident(g5,g6)
    c: Coincident(g6,g7)
    c: Coincident(g7,g4)
    c: Horizontal(g4)
    c: Horizontal(g6)
    c: Vertical(g5)
    c: Vertical(g7)
    c: PointOnObject(g8,g-3)
    c: Vertical(g8)
    c: PointOnObject(g9,g-3)
    c: Vertical(g9)
    c: Symmetric(g2,g1,g9)
    c: Symmetric(g6,g5,g8)
    c: Equal(g2,g6)
    c: DistanceX(g2,g2) = 6
    c: PointOnObject(g0,g-3)
    c: Horizontal(g0,g4)
    c: Horizontal(g1,g6)
    c: PointOnObject(g-4,g9)
    c: PointOnObject(g-5,g8)
    c: DistanceY(g9,g-4) = 3
FEATURE [Sketcher::SketchObject] Sketch017
  AttachmentOffset = pos=(0,0,-52) rot=(0,0,1;0rad)
  ExternalGeometry = -> [Export002,Pocket010]
  FullyConstrained = true
  MapMode = 5
  Placement = pos=(28.44,0,0) rot=(0.57735,0.57735,0.57735;2.0944rad)
  TreeRank = 0
  sketch-geometry (5):
    g0: LineSegment StartX=25 StartY=16.58 StartZ=0 EndX=31 EndY=16.58 EndZ=0
    g1: LineSegment StartX=31 StartY=16.58 StartZ=0 EndX=31 EndY=9.58 EndZ=0
    g2: LineSegment StartX=31 StartY=9.58 StartZ=0 EndX=25 EndY=9.58 EndZ=0
    g3: LineSegment StartX=25 StartY=9.58 StartZ=0 EndX=25 EndY=16.58 EndZ=0
    g4: LineSegment [constr] StartX=28 StartY=9.58 StartZ=0 EndX=28 EndY=12.58 EndZ=0
  constraints (14):
    c: Coincident(g0,g1)
    c: Coincident(g1,g2)
    c: Coincident(g2,g3)
    c: Coincident(g3,g0)
    c: Horizontal(g0)
    c: Horizontal(g2)
    c: Vertical(g1)
    c: Vertical(g3)
    c: Vertical(g4)
    c: Symmetric(g1,g2,g4)
    c: DistanceX(g2,g2) = 6
    c: DistanceY(g4,g4) = 3
    c: Coincident(g4,g-3)
    c: PointOnObject(g0,g-4)
FEATURE [Sketcher::SketchExport] Export001  label="SlotLeft"
  Base = -> Sketch009
  BaseRefs = -> Sketch009 [edge3,edge2,edge4,edge1]
  Placement = pos=(0,0,0) rot=(0.57735,-0.57735,-0.57735;2.0944rad)
  Refs = ;g3.edge3 | ;g2.edge2 | ;g4.edge4 | ;g1.edge1
  SyncPlacement = true
  TreeRank = 0
FEATURE [Sketcher::SketchExport] Export002  label="HoleLeft"
  Base = -> Sketch009
  BaseRefs = -> Sketch009 [edge9]
  Placement = pos=(0,0,0) rot=(0.57735,-0.57735,-0.57735;2.0944rad)
  Refs = ;g9.edge9
  SyncPlacement = true
  TreeRank = 0
FEATURE [PartDesign::Pocket] Pocket
  BaseFeature = -> Pocket007
  ClaimChildren = false
  Fit = 0
  FitJoin = 0
  InnerFit = 0
  InnerFitJoin = 0
  InnerTaperAngle = 0
  InnerTaperAngleRev = 0
  Length = 37
  Length2 = 100
  Linearize = true
  NewSolid = false
  Profile = -> Export002
  Refine = true
  Suppress = false
  TreeRank = 0
  Type = 0
  _ProfileBasedVersion = 1
FEATURE [Sketcher::SketchExport] Export003  label="SlotRight"
  Base = -> Sketch011
  BaseRefs = -> Sketch011 [edge3,edge2,edge4,edge1,edge11,edge10,edge12,edge9]
  Placement = pos=(80.44,0,0) rot=(0.57735,0.57735,0.57735;2.0944rad)
  Refs = ;g3.edge3 | ;g2.edge2 | ;g4.edge4 | ;g1.edge1 | ;g11.edge11 | ;g10.edge10 | ;g12.edge12 | ;g9.edge9
  SyncPlacement = true
  TreeRank = 0
FEATURE [Sketcher::SketchExport] Export004  label="HoleRight"
  Base = -> Sketch011
  BaseRefs = -> Sketch011 [edge18,edge17]
  Placement = pos=(80.44,0,0) rot=(0.57735,0.57735,0.57735;2.0944rad)
  Refs = ;g18.edge18 | ;g17.edge17
  SyncPlacement = true
  TreeRank = 0
FEATURE [PartDesign::Pocket] Pocket010
  BaseFeature = -> Hole
  ClaimChildren = false
  Fit = 0
  FitJoin = 0
  InnerFit = 0
  InnerFitJoin = 0
  InnerTaperAngle = 0
  InnerTaperAngleRev = 0
  Length = 20
  Length2 = 100
  Linearize = true
  NewSolid = false
  Profile = -> Export004
  Refine = true
  Suppress = false
  TreeRank = 0
  Type = 0
  _ProfileBasedVersion = 1
FEATURE [PartDesign::Pocket] Pocket011
  BaseFeature = -> Pocket010
  ClaimChildren = false
  Fit = 0
  FitJoin = 0
  InnerFit = 0
  InnerFitJoin = 0
  InnerTaperAngle = 0
  InnerTaperAngleRev = 0
  Length = 2.2
  Length2 = 100
  Linearize = true
  Midplane = true
  NewSolid = false
  Profile = -> Sketch016
  Refine = true
  Suppress = false
  TreeRank = 0
  Type = 0
  _ProfileBasedVersion = 1
FEATURE [PartDesign::Pocket] Pocket012
  BaseFeature = -> Pocket011
  ClaimChildren = false
  Fit = 0
  FitJoin = 0
  InnerFit = 0
  InnerFitJoin = 0
  InnerTaperAngle = 0
  InnerTaperAngleRev = 0
  Length = 2.2
  Length2 = 100
  Linearize = true
  Midplane = true
  NewSolid = false
  Profile = -> Sketch017
  Refine = true
  Suppress = false
  TreeRank = 0
  Type = 0
  _ProfileBasedVersion = 1
FEATURE [Sketcher::SketchObject] Sketch
  Exports = -> [Export005]
  ExternalGeometry = -> [Chamfer002,Export]
  FullyConstrained = false
  MapMode = 5
  Placement = pos=(0,0,0) rot=(1,0,0;3.14159rad)
  Support = -> [Chamfer002]
  TreeRank = 0
  sketch-geometry (28):
    g0: LineSegment StartX=50.94 StartY=-20.75 StartZ=0 EndX=84.2959 EndY=-20.75 EndZ=0
    g1: LineSegment StartX=84.2959 StartY=-20.75 StartZ=0 EndX=84.2959 EndY=-48 EndZ=0
    g2: LineSegment StartX=84.2959 StartY=-48 StartZ=0 EndX=50.94 EndY=-48 EndZ=0
    g3: LineSegment StartX=-1 StartY=-11.44 StartZ=0 EndX=8.44 EndY=-11.44 EndZ=0
    g4: LineSegment StartX=50.94 StartY=-33.44 StartZ=0 EndX=36.44 EndY=-33.44 EndZ=0
    g5: LineSegment StartX=-1 StartY=-33.44 StartZ=0 EndX=-1 EndY=-11.44 EndZ=0
    g6: LineSegment [constr] StartX=39.44 StartY=-5.44 StartZ=0 EndX=39.44 EndY=-11.44 EndZ=0
    g7: LineSegment [constr] StartX=39.44 StartY=-33.44 StartZ=0 EndX=39.44 EndY=-39.44 EndZ=0
    g8: LineSegment StartX=50.94 StartY=-11.44 StartZ=0 EndX=50.94 EndY=-20.75 EndZ=0
    g9: LineSegment StartX=50.94 StartY=-33.44 StartZ=0 EndX=50.94 EndY=-48 EndZ=0
    g10: LineSegment [constr] StartX=11.44 StartY=1 StartZ=0 EndX=33.44 EndY=1 EndZ=0
    g11: LineSegment [constr] StartX=33.44 StartY=1 StartZ=0 EndX=33.44 EndY=-8.44 EndZ=0
    g12: LineSegment [constr] StartX=33.44 StartY=-67.75 StartZ=0 EndX=11.44 EndY=-67.75 EndZ=0
    g13: LineSegment [constr] StartX=11.44 StartY=-67.75 StartZ=0 EndX=11.44 EndY=-36.44 EndZ=0
    g14: LineSegment StartX=36.44 StartY=-11.44 StartZ=0 EndX=50.94 EndY=-11.44 EndZ=0
    g15: LineSegment [constr] StartX=11.44 StartY=-8.44 StartZ=0 EndX=11.44 EndY=1 EndZ=0
    g16: LineSegment StartX=8.44 StartY=-33.44 StartZ=0 EndX=-1 EndY=-33.44 EndZ=0
    g17: LineSegment [constr] StartX=33.44 StartY=-36.44 StartZ=0 EndX=33.44 EndY=-67.75 EndZ=0
    g18: LineSegment [constr] StartX=39.44 StartY=-5.44 StartZ=0 EndX=33.44 EndY=-5.44 EndZ=0
    g19: LineSegment [constr] StartX=5.44 StartY=-5.44 StartZ=0 EndX=11.44 EndY=-5.44 EndZ=0
    g20: ArcOfCircle [constr] CenterX=8.44 CenterY=-36.44 CenterZ=0 NormalX=0 NormalY=0 NormalZ=1 AngleXU=0 Radius=3 StartAngle=0 EndAngle=1.5708
    g21: ArcOfCircle [constr] CenterX=8.44 CenterY=-8.44 CenterZ=0 NormalX=0 NormalY=0 NormalZ=1 AngleXU=0 Radius=3 StartAngle=4.71239 EndAngle=6.28319
    g22: ArcOfCircle [constr] CenterX=36.44 CenterY=-8.44 CenterZ=0 NormalX=0 NormalY=0 NormalZ=1 AngleXU=0 Radius=3 StartAngle=3.14159 EndAngle=4.71239
    g23: ArcOfCircle [constr] CenterX=36.44 CenterY=-36.44 CenterZ=0 NormalX=0 NormalY=0 NormalZ=1 AngleXU=0 Radius=3 StartAngle=1.5708 EndAngle=3.14159
    g24: LineSegment StartX=8.44 StartY=-11.44 StartZ=0 EndX=36.44 EndY=-11.44 EndZ=0
    g25: LineSegment StartX=8.44 StartY=-33.44 StartZ=0 EndX=36.44 EndY=-33.44 EndZ=0
    g26: LineSegment [constr] StartX=8.44 StartY=-11.44 StartZ=0 EndX=8.44 EndY=-33.44 EndZ=0
    g27: LineSegment [constr] StartX=36.44 StartY=-11.44 StartZ=0 EndX=36.44 EndY=-33.44 EndZ=0
  constraints (70):
    c: Coincident(g0,g1)
    c: Coincident(g1,g2)
    c: Horizontal(g0)
    c: Horizontal(g2)
    c: Vertical(g1)
    c: DistanceY(g0,g-5) = 4
    c: DistanceY(g-4,g2) = 4
    c: Coincident(g16,g5)
    c: Coincident(g5,g3)
    c: Horizontal(g3)
    c: Horizontal(g4)
    c: Vertical(g5)
    c: PointOnObject(g14,g-7)
    c: Tangent(g3,g-7)
    c: Coincident(g6,g-8)
    c: PointOnObject(g6,g3)
    c: Vertical(g6)
    c: PointOnObject(g7,g4)
    c: Coincident(g7,g-9)
    c: Vertical(g7)
    c: Equal(g6,g7)
    c: Coincident(g8,g14)
    c: Coincident(g8,g0)
    c: Vertical(g8)
    c: Coincident(g9,g4)
    c: Coincident(g9,g2)
    c: Vertical(g9)
    c: DistanceX(g3,g-1) = 1
    c: Coincident(g10,g11)
    c: Coincident(g17,g12)
    c: Coincident(g12,g13)
    c: Coincident(g15,g10)
    c: Horizontal(g10)
    c: Horizontal(g12)
    c: Vertical(g11)
    c: Vertical(g13)
    c: Tangent(g3,g14)
    c: Tangent(g13,g15)
    c: Tangent(g4,g16)
    c: Tangent(g11,g17)
    c: Coincident(g18,g-8)
    c: PointOnObject(g18,g11)
    c: Horizontal(g18)
    c: Coincident(g19,g-10)
    c: PointOnObject(g19,g15)
    c: Horizontal(g19)
    c: Equal(g6,g18)
    c: Equal(g18,g19)
    c: DistanceY(g-1,g10) = 1
    c: PointOnObject(g-6,g9)
    c: Tangent(g16,g20) = -1.5708
    c: Tangent(g13,g20) = -1.5708
    c: Tangent(g3,g21) = -1.5708
    c: Tangent(g15,g21) = -1.5708
    c: Tangent(g11,g22) = -1.5708
    c: Tangent(g14,g22) = -1.5708
    c: Tangent(g4,g23) = -1.5708
    c: Tangent(g17,g23) = -1.5708
    c: Radius(g23) = 3
    c: Equal(g23,g20)
    c: Equal(g23,g21)
    c: Equal(g23,g22)
    c: Coincident(g24,g3)
    c: Coincident(g25,g16)
    c: Coincident(g24,g14)
    c: Coincident(g25,g4)
    c: Coincident(g26,g3)
    c: Coincident(g27,g14)
    c: Coincident(g26,g16)
    c: Coincident(g27,g4)
FEATURE [PartDesign::Pocket] Pocket013
  BaseFeature = -> Chamfer002
  ClaimChildren = false
  Fit = 0
  FitJoin = 0
  InnerFit = 0
  InnerFitJoin = 0
  InnerTaperAngle = 0
  InnerTaperAngleRev = 0
  Length = 7
  Length2 = 100
  Linearize = true
  NewSolid = false
  Profile = -> Sketch
  Refine = true
  Suppress = false
  TaperAngle = -10
  TreeRank = 0
  Type = 0
  _ProfileBasedVersion = 1
FEATURE [PartDesign::Fillet] Fillet
  Base = -> Pocket013 [Edge110,Edge105,Edge186]
  BaseFeature = -> Pocket013
  NewSolid = false
  Radius = 1
  Refine = true
  SupportTransform = false
  Suppress = false
  TreeRank = 0
FEATURE [Part::Extrusion] Extrude
  Base = -> Sketch014
  Dir = (0,-1,2e-16)
  DirMode = 2
  FaceMakerClass = Part::FaceMakerBullseye
  InnerTaperAngle = 0
  InnerTaperAngleRev = 0
  LengthFwd = 57
  LengthRev = 0
  Linearize = true
  Reversed = true
  Solid = true
  Symmetric = false
  TreeRank = 0
FEATURE [Part::Cut] Cut
  Base = -> Extrude
  Refine = true
  Tool = -> Extrude001
  TreeRank = 0
FEATURE [Part::FeaturePython] Slice  # WARN: FeaturePython — macro-defined, semantics opaque (R4)
  Base = -> Body001
  Mode = 1
  Tolerance = 0
  Tools = -> [Cut]
  TreeRank = 0
FEATURE [App::DocumentObjectGroup] GrExplode_Slice  label="Exploded Slice"
  ExportMode = 1
  Group = -> [Slice_child0,Slice_child1,Slice_child2,Slice_child3,Slice_child4]
  TreeRank = 0
  _GroupVersion = 1
FEATURE [Part::FeaturePython] Slice_child0  label="E2_Adjustable_Plate_Base"  # WARN: FeaturePython — macro-defined, semantics opaque (R4)
  Base = -> Slice
  FilterType = 1
  Invert = false
  OverrideMaxVal = 0
  TreeRank = 0
  WindowFrom = 80
  WindowTo = 100
  items = 0
FEATURE [Part::FeaturePython] Slice_child1  label="Slice.1"  # WARN: FeaturePython — macro-defined, semantics opaque (R4)
  Base = -> Slice
  FilterType = 1
  Invert = false
  OverrideMaxVal = 0
  TreeRank = 0
  WindowFrom = 80
  WindowTo = 100
  items = 1
FEATURE [Part::FeaturePython] Slice_child2  label="Slice.2"  # WARN: FeaturePython — macro-defined, semantics opaque (R4)
  Base = -> Slice
  FilterType = 1
  Invert = false
  OverrideMaxVal = 0
  TreeRank = 0
  WindowFrom = 80
  WindowTo = 100
  items = 2
FEATURE [Part::FeaturePython] Slice_child3  label="E2_Left_Keyway_Base"  # WARN: FeaturePython — macro-defined, semantics opaque (R4)
  Base = -> Slice
  FilterType = 1
  Invert = false
  OverrideMaxVal = 0
  TreeRank = 0
  WindowFrom = 80
  WindowTo = 100
  items = 3
FEATURE [Part::FeaturePython] Slice_child4  label="E2_Right_Keyway_Base"  # WARN: FeaturePython — macro-defined, semantics opaque (R4)
  Base = -> Slice
  FilterType = 1
  Invert = false
  OverrideMaxVal = 0
  TreeRank = 0
  WindowFrom = 80
  WindowTo = 100
  items = 4
FEATURE [Sketcher::SketchExport] Export005
  Base = -> Sketch
  BaseRefs = -> Sketch [edge22,edge16,edge11,edge12,edge23,edge28,edge27,edge21,edge24,edge18,edge14,edge13]
  Placement = pos=(0,0,0) rot=(1,0,0;3.14159rad)
  Refs = ;g32.edge22 | ;g24.edge16 | ;g19.edge11 | ;g20.edge12 | ;g33.edge23 | ;g38.edge28 | ;g37.edge27 | ;g31.edge21 | ;g34.edge24 | ;g26.edge18 | ;g22.edge14 | ;g21.edge13
  SyncPlacement = true
  TreeRank = 0
FEATURE [PartDesign::Pocket] Pocket014
  BaseFeature = -> Fillet
  ClaimChildren = false
  Fit = 0
  FitJoin = 0
  InnerFit = 0
  InnerFitJoin = 0
  InnerTaperAngle = 0
  InnerTaperAngleRev = 0
  Length = 6.8
  Length2 = 100
  Linearize = true
  NewSolid = false
  Profile = -> Export005
  Refine = true
  Suppress = false
  TaperAngle = -10
  TreeRank = 0
  Type = 0
  _ProfileBasedVersion = 1
FEATURE [PartDesign::Body] Body  label="E2_Adjustable_Plate"
  AutoGroupSolids = false
  BaseFeature = -> Slice_child0
  ExportMode = 0
  Group = -> [BaseFeature,Sketch018,Pocket015,Sketch019,Pocket016]
  Origin = -> Origin
  Tip = -> Pocket016
  TreeRank = 0
  _ExportChildren = -> [BaseFeature,Pocket015,Pocket016]
  _GroupVersion = 1
FEATURE [PartDesign::FeatureBase] BaseFeature
  BaseFeature = -> Slice_child0
  NewSolid = false
  Suppress = false
  TreeRank = 0
FEATURE [Sketcher::SketchObject] Sketch018
  ExternalGeometry = -> [BaseFeature]
  FullyConstrained = true
  MapMode = 5
  Placement = pos=(0,0,0) rot=(0.57735,-0.57735,-0.57735;2.0944rad)
  Support = -> [BaseFeature]
  TreeRank = 0
  sketch-geometry (4):
    g0: ArcOfCircle CenterX=-25 CenterY=12.58 CenterZ=0 NormalX=0 NormalY=0 NormalZ=1 AngleXU=0 Radius=1.5 StartAngle=4.71239 EndAngle=7.85398
    g1: ArcOfCircle CenterX=-28 CenterY=12.58 CenterZ=0 NormalX=0 NormalY=0 NormalZ=1 AngleXU=0 Radius=1.5 StartAngle=1.5708 EndAngle=4.71239
    g2: LineSegment StartX=-25 StartY=14.08 StartZ=0 EndX=-28 EndY=14.08 EndZ=0
    g3: LineSegment StartX=-25 StartY=11.08 StartZ=0 EndX=-28 EndY=11.08 EndZ=0
  constraints (9):
    c: Tangent(g0,g3) = 1.5708
    c: Tangent(g0,g2) = -1.5708
    c: Tangent(g2,g1) = -1.5708
    c: Tangent(g3,g1) = 1.5708
    c: Horizontal(g2)
    c: Equal(g0,g1)
    c: Coincident(g0,g-4)
    c: PointOnObject(g1,g-3)
    c: Tangent(g-3,g3)
FEATURE [PartDesign::Pocket] Pocket015
  BaseFeature = -> BaseFeature
  ClaimChildren = false
  Fit = 0
  FitJoin = 0
  InnerFit = 0
  InnerFitJoin = 0
  InnerTaperAngle = 0
  InnerTaperAngleRev = 0
  Length = 37
  Length2 = 100
  Linearize = true
  NewSolid = false
  Profile = -> Sketch018
  Refine = true
  Suppress = false
  TreeRank = 0
  Type = 0
  _ProfileBasedVersion = 1
FEATURE [Sketcher::SketchObject] Sketch019
  ExternalGeometry = -> [Pocket015]
  FullyConstrained = true
  MapMode = 5
  Placement = pos=(80.44,0,0) rot=(0.57735,0.57735,0.57735;2.0944rad)
  Support = -> [Pocket015]
  TreeRank = 0
  sketch-geometry (8):
    g0: ArcOfCircle CenterX=6.5 CenterY=12.58 CenterZ=0 NormalX=0 NormalY=0 NormalZ=1 AngleXU=0 Radius=1.5 StartAngle=1.5708 EndAngle=4.71239
    g1: ArcOfCircle CenterX=9.5 CenterY=12.58 CenterZ=0 NormalX=0 NormalY=0 NormalZ=1 AngleXU=0 Radius=1.5 StartAngle=4.71239 EndAngle=7.85398
    g2: LineSegment StartX=6.5 StartY=11.08 StartZ=0 EndX=9.5 EndY=11.08 EndZ=0
    g3: LineSegment StartX=6.5 StartY=14.08 StartZ=0 EndX=9.5 EndY=14.08 EndZ=0
    g4: ArcOfCircle CenterX=41.5 CenterY=12.58 CenterZ=0 NormalX=0 NormalY=0 NormalZ=1 AngleXU=0 Radius=1.5 StartAngle=1.5708 EndAngle=4.71239
    g5: ArcOfCircle CenterX=44.5 CenterY=12.58 CenterZ=0 NormalX=0 NormalY=0 NormalZ=1 AngleXU=0 Radius=1.5 StartAngle=4.71239 EndAngle=7.85398
    g6: LineSegment StartX=41.5 StartY=11.08 StartZ=0 EndX=44.5 EndY=11.08 EndZ=0
    g7: LineSegment StartX=41.5 StartY=14.08 StartZ=0 EndX=44.5 EndY=14.08 EndZ=0
  constraints (18):
    c: Tangent(g0,g3) = 1.5708
    c: Tangent(g0,g2) = -1.5708
    c: Tangent(g2,g1) = -1.5708
    c: Tangent(g3,g1) = 1.5708
    c: Horizontal(g2)
    c: Equal(g0,g1)
    c: Coincident(g0,g-3)
    c: Tangent(g4,g7) = 1.5708
    c: Tangent(g4,g6) = -1.5708
    c: Tangent(g6,g5) = -1.5708
    c: Tangent(g7,g5) = 1.5708
    c: Horizontal(g6)
    c: Equal(g4,g5)
    c: Coincident(g4,g-5)
    c: Equal(g5,g-6)
    c: Equal(g1,g-4)
    c: Vertical(g1,g-4)
    c: Vertical(g5,g-6)
FEATURE [PartDesign::Pocket] Pocket016
  BaseFeature = -> Pocket015
  ClaimChildren = false
  Fit = 0
  FitJoin = 0
  InnerFit = 0
  InnerFitJoin = 0
  InnerTaperAngle = 0
  InnerTaperAngleRev = 0
  Length = 22
  Length2 = 100
  Linearize = true
  NewSolid = false
  Profile = -> Sketch019
  Refine = true
  Suppress = false
  TreeRank = 0
  Type = 0
  _ProfileBasedVersion = 1
FEATURE [PartDesign::Body] Body002  label="E2_Left_Keyway"
  AutoGroupSolids = false
  BaseFeature = -> Slice_child3
  ExportMode = 0
  Group = -> [BaseFeature001,Sketch020,Pocket017,Sketch022,Pocket019]
  Origin = -> Origin002
  Tip = -> Pocket019
  TreeRank = 13
  _ExportChildren = -> [BaseFeature001,Pocket017,Pocket019]
  _GroupVersion = 1
FEATURE [PartDesign::FeatureBase] BaseFeature001
  BaseFeature = -> Slice_child3
  NewSolid = false
  Suppress = false
  TreeRank = 10
FEATURE [PartDesign::Body] Body003  label="E2_Right_Keyway"
  AutoGroupSolids = false
  BaseFeature = -> Slice_child4
  ExportMode = 0
  Group = -> [BaseFeature002,Sketch021,Pocket018,Sketch023,Pocket020]
  Origin = -> Origin003
  Tip = -> Pocket020
  TreeRank = 26
  _ExportChildren = -> [BaseFeature002,Pocket018,Pocket020]
  _GroupVersion = 1
FEATURE [PartDesign::FeatureBase] BaseFeature002
  BaseFeature = -> Slice_child4
  NewSolid = false
  Suppress = false
  TreeRank = 23
FEATURE [Sketcher::SketchObject] Sketch020
  ExternalGeometry = -> [BaseFeature001]
  FullyConstrained = true
  MapMode = 5
  Placement = pos=(0,-1.9e-15,8.78) rot=(1,0,0;3.14159rad)
  Support = -> [BaseFeature001]
  TreeRank = 27
  sketch-geometry (2):
    g0: Circle CenterX=68.44 CenterY=-16.75 CenterZ=0 NormalX=0 NormalY=0 NormalZ=1 AngleXU=0 Radius=2.85
    g1: Circle CenterX=68.44 CenterY=-52 CenterZ=0 NormalX=0 NormalY=0 NormalZ=1 AngleXU=0 Radius=2.85
  constraints (4):
    c: Coincident(g0,g-3)
    c: Coincident(g1,g-4)
    c: Diameter(g1) = 5.7
    c: Equal(g1,g0)
FEATURE [PartDesign::Pocket] Pocket017
  BaseFeature = -> BaseFeature001
  ClaimChildren = false
  Fit = 0
  FitJoin = 0
  InnerFit = 0
  InnerFitJoin = 0
  InnerTaperAngle = 0
  InnerTaperAngleRev = 0
  Length = 6
  Length2 = 100
  Linearize = true
  NewSolid = false
  Profile = -> Sketch020
  Refine = true
  Suppress = false
  TreeRank = 28
  Type = 0
  _ProfileBasedVersion = 1
FEATURE [Sketcher::SketchObject] Sketch021
  ExternalGeometry = -> [BaseFeature002]
  FullyConstrained = true
  MapMode = 5
  Placement = pos=(0,-1.9e-15,8.78) rot=(1,0,0;3.14159rad)
  Support = -> [BaseFeature002]
  TreeRank = 29
  sketch-geometry (2):
    g0: Circle CenterX=28.44 CenterY=-16.75 CenterZ=0 NormalX=0 NormalY=0 NormalZ=1 AngleXU=0 Radius=2.85
    g1: Circle CenterX=28.44 CenterY=-52 CenterZ=0 NormalX=0 NormalY=0 NormalZ=1 AngleXU=0 Radius=2.85
  constraints (4):
    c: Coincident(g0,g-3)
    c: Coincident(g1,g-4)
    c: Diameter(g1) = 5.7
    c: Equal(g1,g0)
FEATURE [PartDesign::Pocket] Pocket018
  BaseFeature = -> BaseFeature002
  ClaimChildren = false
  Fit = 0
  FitJoin = 0
  InnerFit = 0
  InnerFitJoin = 0
  InnerTaperAngle = 0
  InnerTaperAngleRev = 0
  Length = 6
  Length2 = 100
  Linearize = true
  NewSolid = false
  Profile = -> Sketch021
  Refine = true
  Suppress = false
  TreeRank = 30
  Type = 0
  _ProfileBasedVersion = 1
FEATURE [Sketcher::SketchObject] Sketch022
  ExternalGeometry = -> [Pocket017]
  FullyConstrained = true
  MapMode = 5
  Placement = pos=(1.5e-15,-3.2e-15,14.78) rot=(1,0,0;3.14159rad)
  Support = -> [Pocket017]
  TreeRank = 31
  sketch-geometry (10):
    g0: Circle [constr] CenterX=68.44 CenterY=-52 CenterZ=0 NormalX=0 NormalY=0 NormalZ=1 AngleXU=0 Radius=1.661
    g1: LineSegment StartX=66.779 StartY=-49.6841 StartZ=0 EndX=66.779 EndY=-54.3159 EndZ=0
    g2: LineSegment StartX=70.101 StartY=-49.6841 StartZ=0 EndX=70.101 EndY=-54.3159 EndZ=0
    g3: ArcOfCircle CenterX=68.44 CenterY=-52 CenterZ=0 NormalX=0 NormalY=0 NormalZ=1 AngleXU=0 Radius=2.85 StartAngle=0.948618 EndAngle=2.19298
    g4: ArcOfCircle CenterX=68.44 CenterY=-52 CenterZ=0 NormalX=0 NormalY=0 NormalZ=1 AngleXU=0 Radius=2.85 StartAngle=4.09021 EndAngle=5.33457
    g5: Circle [constr] CenterX=68.44 CenterY=-16.75 CenterZ=0 NormalX=0 NormalY=0 NormalZ=1 AngleXU=0 Radius=1.661
    g6: LineSegment StartX=66.779 StartY=-14.4341 StartZ=0 EndX=66.779 EndY=-19.0659 EndZ=0
    g7: LineSegment StartX=70.101 StartY=-14.4341 StartZ=0 EndX=70.101 EndY=-19.0659 EndZ=0
    g8: ArcOfCircle CenterX=68.44 CenterY=-16.75 CenterZ=0 NormalX=0 NormalY=0 NormalZ=1 AngleXU=0 Radius=2.85 StartAngle=0.948618 EndAngle=2.19298
    g9: ArcOfCircle CenterX=68.44 CenterY=-16.75 CenterZ=0 NormalX=0 NormalY=0 NormalZ=1 AngleXU=0 Radius=2.85 StartAngle=4.09021 EndAngle=5.33457
  constraints (29):
    c: Coincident(g0,g-5)
    c: PointOnObject(g-5,g0)
    c: PointOnObject(g1,g-4)
    c: PointOnObject(g1,g-4)
    c: Vertical(g1)
    c: Tangent(g1,g0)
    c: PointOnObject(g2,g-4)
    c: Coincident(g3,g1)
    c: Coincident(g4,g3)
    c: Coincident(g2,g3)
    c: Coincident(g4,g1)
    c: Coincident(g2,g4)
    c: Tangent(g2,g0)
    c: Vertical(g2)
    c: Equal(g4,g-4)
    c: Coincident(g5,g-6)
    c: PointOnObject(g-6,g5)
    c: PointOnObject(g6,g-3)
    c: PointOnObject(g6,g-3)
    c: Vertical(g6)
    c: Vertical(g7)
    c: Coincident(g8,g-6)
    c: Coincident(g9,g8)
    c: Coincident(g9,g6)
    c: Coincident(g8,g7)
    c: Coincident(g6,g8)
    c: Coincident(g9,g7)
    c: Tangent(g7,g5)
    c: Tangent(g6,g5)
FEATURE [PartDesign::Pocket] Pocket019
  BaseFeature = -> Pocket017
  ClaimChildren = false
  Fit = 0
  FitJoin = 0
  InnerFit = 0
  InnerFitJoin = 0
  InnerTaperAngle = 0
  InnerTaperAngleRev = 0
  Length = 0.2
  Length2 = 100
  Linearize = true
  NewSolid = false
  Profile = -> Sketch022
  Refine = true
  Suppress = false
  TreeRank = 32
  Type = 0
  _ProfileBasedVersion = 1
FEATURE [Sketcher::SketchObject] Sketch023
  ExternalGeometry = -> [Pocket018]
  FullyConstrained = true
  MapMode = 5
  Placement = pos=(-1.5e-15,-3.5e-15,14.78) rot=(1,0,0;3.14159rad)
  Support = -> [Pocket018]
  TreeRank = 36
  sketch-geometry (10):
    g0: Circle [constr] CenterX=28.44 CenterY=-16.75 CenterZ=0 NormalX=0 NormalY=0 NormalZ=1 AngleXU=0 Radius=1.661
    g1: LineSegment StartX=26.779 StartY=-14.4341 StartZ=0 EndX=26.779 EndY=-19.0659 EndZ=0
    g2: LineSegment StartX=30.101 StartY=-14.4341 StartZ=0 EndX=30.101 EndY=-19.0659 EndZ=0
    g3: ArcOfCircle CenterX=28.44 CenterY=-16.75 CenterZ=0 NormalX=0 NormalY=0 NormalZ=1 AngleXU=0 Radius=2.85 StartAngle=0.948618 EndAngle=2.19298
    g4: ArcOfCircle CenterX=28.44 CenterY=-16.75 CenterZ=0 NormalX=0 NormalY=0 NormalZ=1 AngleXU=0 Radius=2.85 StartAngle=4.09021 EndAngle=5.33457
    g5: Circle [constr] CenterX=28.44 CenterY=-52 CenterZ=0 NormalX=0 NormalY=0 NormalZ=1 AngleXU=0 Radius=1.661
    g6: LineSegment StartX=26.779 StartY=-49.6841 StartZ=0 EndX=26.779 EndY=-54.3159 EndZ=0
    g7: LineSegment StartX=30.101 StartY=-49.6841 StartZ=0 EndX=30.101 EndY=-54.3159 EndZ=0
    g8: ArcOfCircle CenterX=28.44 CenterY=-52 CenterZ=0 NormalX=0 NormalY=0 NormalZ=1 AngleXU=0 Radius=2.85 StartAngle=0.948618 EndAngle=2.19298
    g9: ArcOfCircle CenterX=28.44 CenterY=-52 CenterZ=0 NormalX=0 NormalY=0 NormalZ=1 AngleXU=0 Radius=2.85 StartAngle=4.09021 EndAngle=5.33457
  constraints (28):
    c: Coincident(g0,g-4)
    c: PointOnObject(g-4,g0)
    c: PointOnObject(g1,g-3)
    c: PointOnObject(g1,g-3)
    c: Vertical(g1)
    c: Tangent(g1,g0)
    c: Vertical(g2)
    c: Coincident(g3,g-4)
    c: Coincident(g3,g1)
    c: Coincident(g3,g2)
    c: Coincident(g4,g3)
    c: Coincident(g4,g1)
    c: Coincident(g4,g2)
    c: Tangent(g2,g0)
    c: Coincident(g5,g-6)
    c: PointOnObject(g-6,g5)
    c: PointOnObject(g6,g-5)
    c: PointOnObject(g6,g-5)
    c: Vertical(g6)
    c: Vertical(g7)
    c: Coincident(g8,g-6)
    c: Coincident(g8,g6)
    c: Coincident(g8,g7)
    c: Coincident(g9,g8)
    c: Coincident(g9,g6)
    c: Coincident(g9,g7)
    c: Tangent(g7,g5)
    c: Tangent(g6,g5)
FEATURE [PartDesign::Pocket] Pocket020
  BaseFeature = -> Pocket018
  ClaimChildren = false
  Fit = 0
  FitJoin = 0
  InnerFit = 0
  InnerFitJoin = 0
  InnerTaperAngle = 0
  InnerTaperAngleRev = 0
  Length = 0.2
  Length2 = 100
  Linearize = true
  NewSolid = false
  Profile = -> Sketch023
  Refine = true
  Suppress = false
  TreeRank = 37
  Type = 0
  _ProfileBasedVersion = 1
